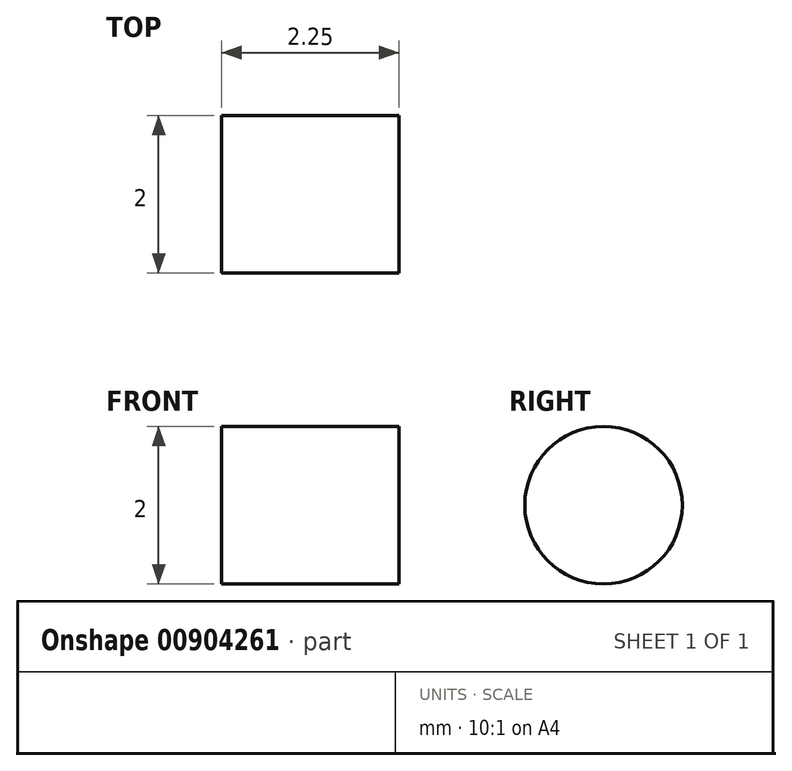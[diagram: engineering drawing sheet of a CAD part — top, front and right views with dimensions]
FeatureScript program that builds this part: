
annotation { "Feature Type Name" : "Feature", "Feature Type Description" : "" }
export const myFeature = defineFeature(function(context is Context, id is Id, definition is map)
    precondition{}
    {
        {
            var Q0;
            Q0=qCreatedBy(makeId("Front.planeOp"),FACE);
            var sketch = newSketch(context, id + "F0", { "sketchPlane" : qUnion([Q0])});
            skLineSegment(sketch, "E0.bottom", {"start": v(0, 0) * mm, "end": v(-1.25, 0) * mm});
            skLineSegment(sketch, "E0.top", {"start": v(0, 1) * mm, "end": v(-1.25, 1) * mm});
            skLineSegment(sketch, "E0.left", {"start": v(0, 0) * mm, "end": v(0, 1) * mm});
            skLineSegment(sketch, "E0.right", {"start": v(-1.25, 0) * mm, "end": v(-1.25, 1) * mm});
            skLineSegment(sketch, "E1.bottom", {"start": v(-1.25, 0) * mm, "end": v(-1.75, 0) * mm});
            skLineSegment(sketch, "E1.top", {"start": v(-1.25, 1) * mm, "end": v(-1.75, 1) * mm});
            skLineSegment(sketch, "E1.right", {"start": v(-1.75, 0) * mm, "end": v(-1.75, 1) * mm});
            skLineSegment(sketch, "E2.bottom", {"start": v(0, 0) * mm, "end": v(0.5, 0) * mm});
            skLineSegment(sketch, "E2.top", {"start": v(0, 1) * mm, "end": v(0.5, 1) * mm});
            skLineSegment(sketch, "E2.right", {"start": v(0.5, 0) * mm, "end": v(0.5, 1) * mm});
            skSolve(sketch);
        }
        {
            var Q0;
            Q0=makeQuery(id+"F0.imprint","IMPRINT",FACE,{"disambiguationData":[TD([[makeQuery(id+"F0.imprint","IMPRINT",EDGE,{"derivedFrom":sQuery(id+"F0.wireOp",EDGE,"E0.bottom")}),-1.0]])]});
            var Q1;
            Q1=makeQuery(id+"F0.imprint","IMPRINT",FACE,{"disambiguationData":[TD([[makeQuery(id+"F0.imprint","IMPRINT",EDGE,{"derivedFrom":sQuery(id+"F0.wireOp",EDGE,"E1.bottom")}),-1.0]])]});
            var Q2;
            Q2=makeQuery(id+"F0.imprint","IMPRINT",FACE,{"disambiguationData":[TD([[makeQuery(id+"F0.imprint","IMPRINT",EDGE,{"derivedFrom":sQuery(id+"F0.wireOp",EDGE,"E2.bottom")}),1.0]])]});
            var Q3;
            Q3=sQuery(id+"F0.wireOp",EDGE,"E0.bottom");
            revolve(context, id + "F1", {"surfaceOperationType" : NewSurfaceOperationType.NEW, "entities" : qUnion([Q0, Q1, Q2]), "axis" : qUnion([Q3]), "revolveType" : RevolveType.FULL});
        }
    });
